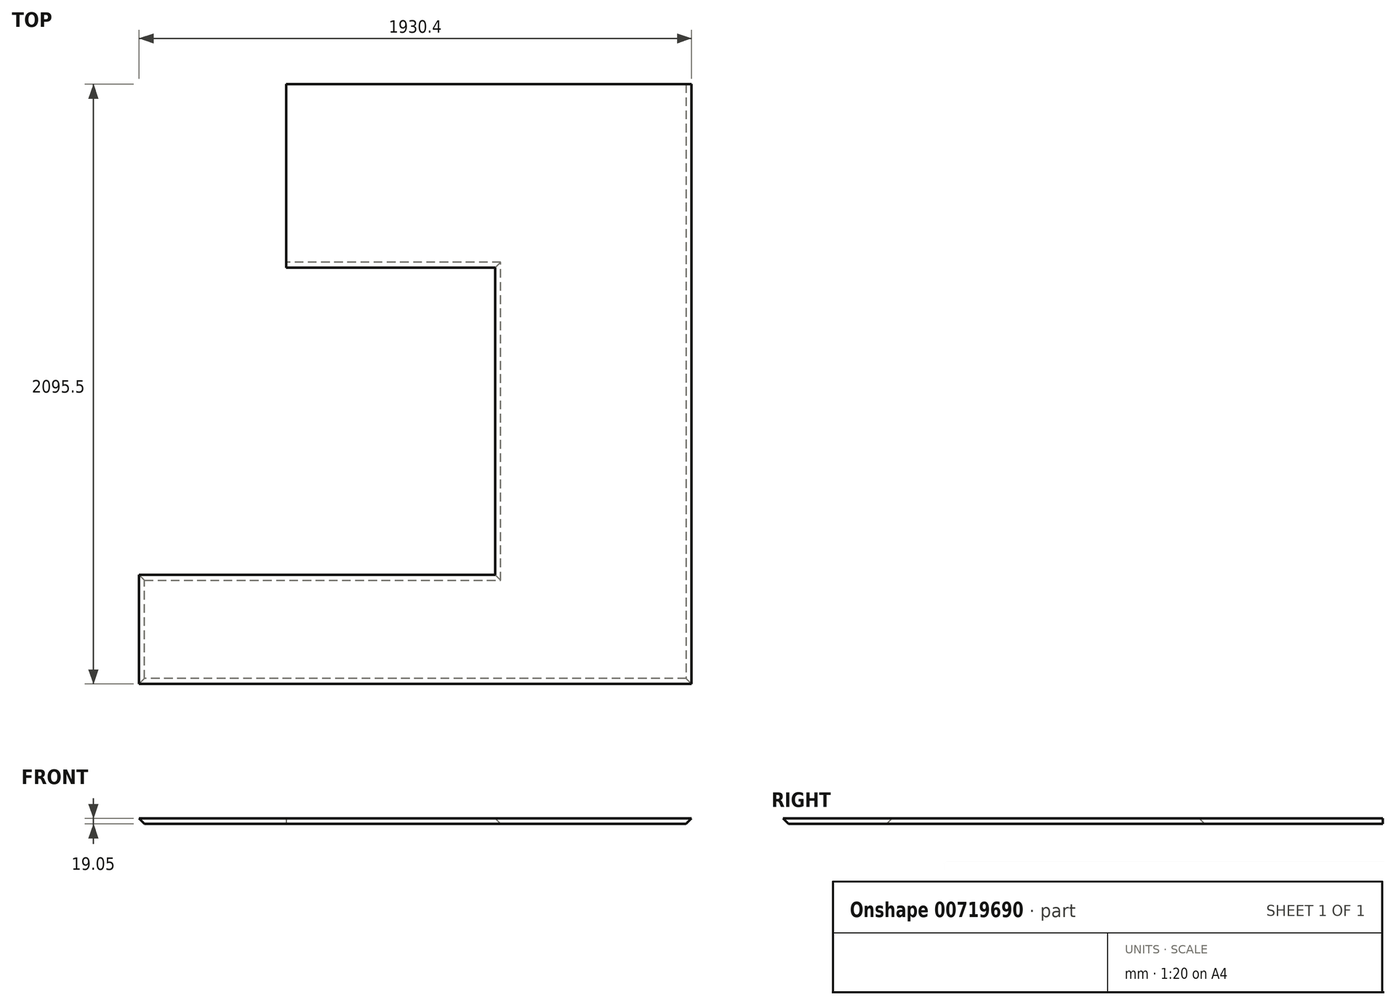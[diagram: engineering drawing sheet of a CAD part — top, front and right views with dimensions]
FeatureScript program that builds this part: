
annotation { "Feature Type Name" : "Feature", "Feature Type Description" : "" }
export const myFeature = defineFeature(function(context is Context, id is Id, definition is map)
    precondition{}
    {
        {
            var Q0;
            Q0=qCreatedBy(makeId("Top.planeOp"),FACE);
            var sketch = newSketch(context, id + "F0", { "sketchPlane" : qUnion([Q0])});
            skLineSegment(sketch, "E0", {"start": v(0, 0) * mm, "end": v(0, -381) * mm});
            skLineSegment(sketch, "E1", {"start": v(0, -381) * mm, "end": v(1930.4, -381) * mm});
            skLineSegment(sketch, "E2", {"start": v(1930.4, -381) * mm, "end": v(1930.4, 1714.5) * mm});
            skLineSegment(sketch, "E3", {"start": v(1930.4, 1714.5) * mm, "end": v(514.35, 1714.5) * mm});
            skLineSegment(sketch, "E4", {"start": v(514.35, 1073.15) * mm, "end": v(1244.6, 1073.15) * mm});
            skLineSegment(sketch, "E5", {"start": v(1244.6, 1073.15) * mm, "end": v(1244.6, 0) * mm});
            skLineSegment(sketch, "E6", {"start": v(1244.6, 0) * mm, "end": v(0, 0) * mm});
            skLineSegment(sketch, "E7", {"start": v(514.35, 1714.5) * mm, "end": v(514.35, 1073.15) * mm});
            skSolve(sketch);
        }
        {
            var Q0;
            Q0=makeQuery(id+"F0.imprint","IMPRINT",FACE,{"disambiguationData":[TD([[makeQuery(id+"F0.imprint","IMPRINT",EDGE,{"derivedFrom":sQuery(id+"F0.wireOp",EDGE,"E0")}),1.0]])]});
            extrude(context, id + "F1", {"entities" : qUnion([Q0]), "depth" : 19.05 * mm, "offsetDistance" : 25.4 * mm});
        }
        {
            var Q0;
            Q0=makeQuery(id+"F1.opExtrude","CAP_EDGE",EDGE,{"disambiguationData":[OSD([sQuery(id+"F0.wireOp",EDGE,"E1")])],"isStart":true});
            var Q1;
            Q1=makeQuery(id+"F1.opExtrude","CAP_EDGE",EDGE,{"disambiguationData":[OSD([sQuery(id+"F0.wireOp",EDGE,"E2")])],"isStart":true});
            var Q2;
            Q2=makeQuery(id+"F1.opExtrude","CAP_EDGE",EDGE,{"disambiguationData":[OSD([sQuery(id+"F0.wireOp",EDGE,"E4")])],"isStart":true});
            var Q3;
            Q3=makeQuery(id+"F1.opExtrude","CAP_EDGE",EDGE,{"disambiguationData":[OSD([sQuery(id+"F0.wireOp",EDGE,"E5")])],"isStart":true});
            var Q4;
            Q4=makeQuery(id+"F1.opExtrude","CAP_EDGE",EDGE,{"disambiguationData":[OSD([sQuery(id+"F0.wireOp",EDGE,"E6")])],"isStart":true});
            var Q5;
            Q5=makeQuery(id+"F1.opExtrude","CAP_EDGE",EDGE,{"disambiguationData":[OSD([sQuery(id+"F0.wireOp",EDGE,"E0")])],"isStart":true});
            chamfer(context, id + "F2", {"entities" : qUnion([Q0, Q1, Q2, Q3, Q4, Q5]), "width" : 19.05 * mm, "tangentPropagation" : true});
        }
    });
